# Revit family: 380140001_Griflex Lavamanos-Lavaplatos De 40cm
name_source: partatom
category: Pipe Accessories
units: mm (PartAtom-declared; Revit-internal decimal feet)

## family parameters
Always vertical = Yes
Cut with Voids When Loaded = No
OmniClass Number = 23.27.43.00
OmniClass Title = Pipe Fittings
Part Type = Normal
Round Connector Dimension = Use Diameter
Shared = No
Work Plane-Based = No

## types (1)
- 380140001_Griflex Lavamanos-Lavaplatos De 40cm
    Depth = 150 mm
    Description = Adquiere ahora el conector plástico de alta flexibilidad para lavamanos o lavaplatos, cuenta con acabados en blanco mate. Está fabricado en plástico flexible y hecho con los más altos estándares de calidad.
    Diameter = 13 mm
    Gross Weight approx = 14 gr. (0,0309 lb.)
    Height = 250 mm  [stored 0.82021 ft]
    Intermittent impulse pressure (Life Cycle) = 100.000 Ciclos
    Material = Corona_Plastico_Blanco
    Maximum working pressure (gauge) = 125 Psi
    Minimum pressure = Presión mínima 20 Psi
    Net Weight approx = 10gr. (0.0220  lb.)
    Radius = 100 mm  [stored 0.328084 ft]
    URL = https://corona.co
    Warranty = 5 years
    Work Temperature = 4ºC - 71ºC (39,2ºF - 160ºF).

note: [stored X ft] marks values corroborated as IEEE doubles in the binary element streams (Revit-internal decimal feet)

## geometry (parser evidence)
native form markers: Sweep x7
no freeform markers — native parametric forms only
